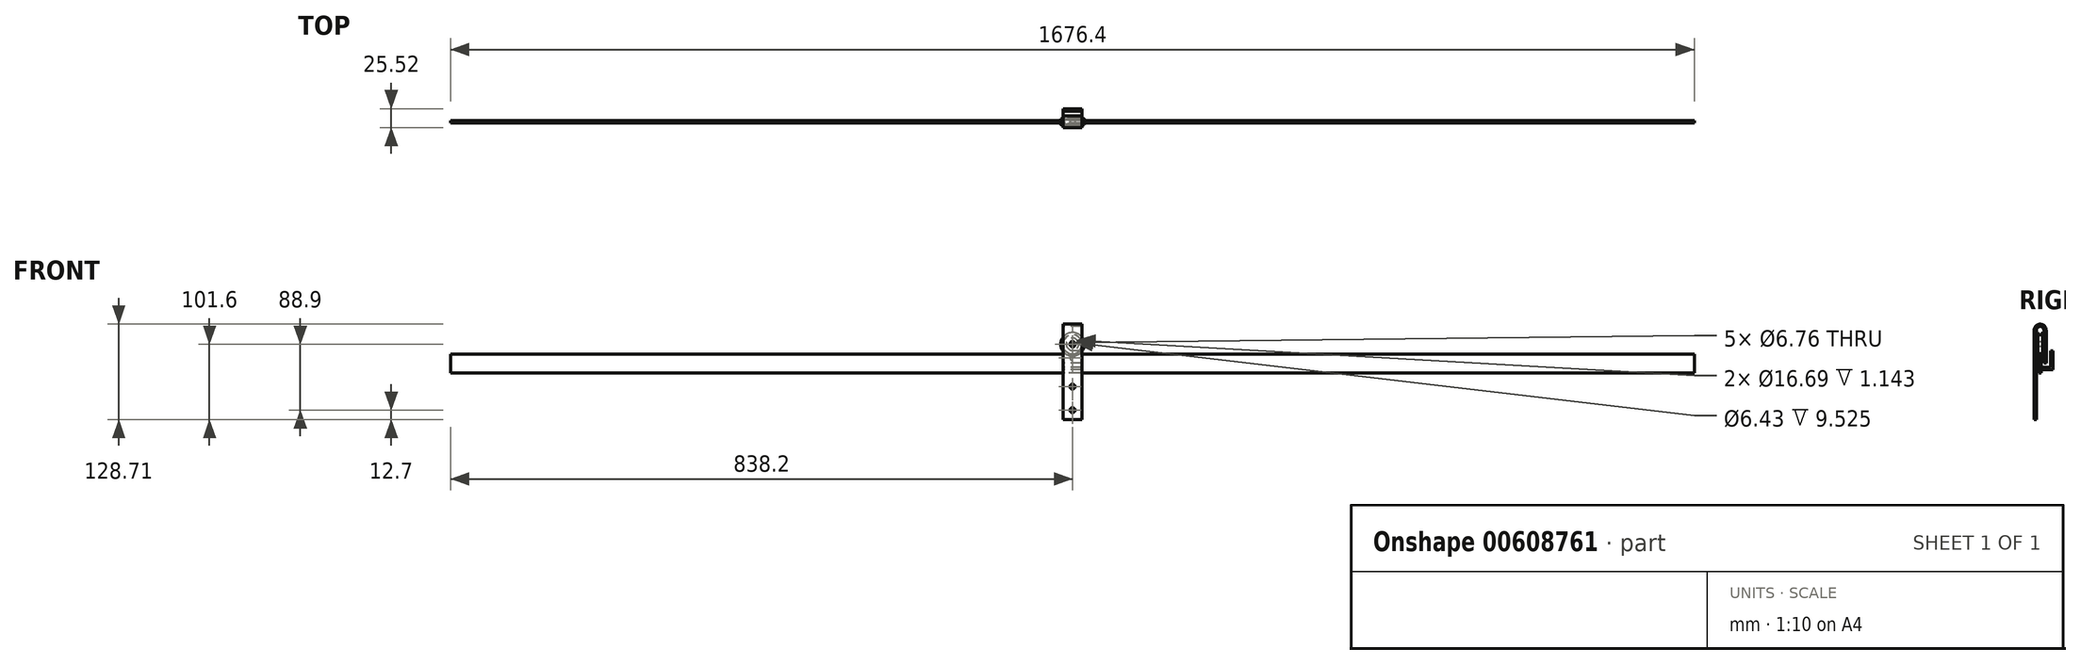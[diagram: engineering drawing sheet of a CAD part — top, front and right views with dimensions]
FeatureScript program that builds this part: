
annotation { "Feature Type Name" : "Feature", "Feature Type Description" : "" }
export const myFeature = defineFeature(function(context is Context, id is Id, definition is map)
    precondition{}
    {
        {
            var Q0;
            Q0=qCreatedBy(makeId("Right.planeOp"),FACE);
            var sketch = newSketch(context, id + "F0", { "sketchPlane" : qUnion([Q0])});
            skLineSegment(sketch, "E0", {"start": v(-9, 0) * mm, "end": v(10.82, 0) * mm, "construction": true});
            skLineSegment(sketch, "E1", {"start": v(-4.76, 3.21) * mm, "end": v(4.76, 3.21) * mm});
            skLineSegment(sketch, "E2", {"start": v(4.76, 3.21) * mm, "end": v(4.76, 4.57) * mm});
            skLineSegment(sketch, "E3", {"start": v(4.76, 4.57) * mm, "end": v(2.97, 4.57) * mm});
            skLineSegment(sketch, "E4", {"start": v(2.97, 4.57) * mm, "end": v(2.97, 8.34) * mm});
            skLineSegment(sketch, "E5", {"start": v(2.97, 8.34) * mm, "end": v(4.11, 8.34) * mm});
            skLineSegment(sketch, "E6", {"start": v(4.11, 8.34) * mm, "end": v(4.11, 15.88) * mm});
            skLineSegment(sketch, "E7", {"start": v(4.11, 15.88) * mm, "end": v(2.97, 15.88) * mm});
            skLineSegment(sketch, "E8", {"start": v(0, 0) * mm, "end": v(0, 15.88) * mm, "construction": true});
            skArc(sketch, "E9", {"start": v(-2.97, 15.88) * mm, "mid": v(0, 12.9) * mm, "end": v(2.97, 15.88) * mm});
            skLineSegment(sketch, "E10", {"start": v(-2.97, 15.88) * mm, "end": v(-4.11, 15.88) * mm});
            skLineSegment(sketch, "E11", {"start": v(-4.11, 15.88) * mm, "end": v(-4.11, 8.34) * mm});
            skLineSegment(sketch, "E12", {"start": v(-4.11, 8.34) * mm, "end": v(-2.97, 8.34) * mm});
            skLineSegment(sketch, "E13", {"start": v(-2.97, 8.34) * mm, "end": v(-2.97, 4.57) * mm});
            skLineSegment(sketch, "E14", {"start": v(-2.97, 4.57) * mm, "end": v(-4.76, 4.57) * mm});
            skLineSegment(sketch, "E15", {"start": v(-4.76, 4.57) * mm, "end": v(-4.76, 3.21) * mm});
            skSolve(sketch);
        }
        {
            var Q0;
            Q0 = qSketchRegion(id + "F0", true);
            var Q1;
            Q1=sQuery(id+"F0.wireOp",EDGE,"E0");
            revolve(context, id + "F1", {"entities" : qUnion([Q0]), "axis" : qUnion([Q1]), "revolveType" : RevolveType.FULL});
        }
        {
            var Q0;
            Q0=qCreatedBy(makeId("Right.planeOp"),FACE);
            var sketch = newSketch(context, id + "F2", { "sketchPlane" : qUnion([Q0])});
            skLineSegment(sketch, "E16.bottom", {"start": v(1.59, -38.89) * mm, "end": v(-1.59, -38.89) * mm});
            skLineSegment(sketch, "E16.top", {"start": v(1.59, -13.49) * mm, "end": v(-1.59, -13.49) * mm});
            skLineSegment(sketch, "E16.left", {"start": v(1.59, -38.89) * mm, "end": v(1.59, -13.49) * mm});
            skLineSegment(sketch, "E16.right", {"start": v(-1.59, -38.89) * mm, "end": v(-1.59, -13.49) * mm});
            skPoint(sketch, "E16.middle", {"position": v(0, -26.19) * mm});
            skLineSegment(sketch, "E17", {"start": v(4.89, -25.4) * mm, "end": v(4.89, 19.05) * mm});
            skArc(sketch, "E18", {"start": v(4.89, 19.05) * mm, "mid": v(0, 23.94) * mm, "end": v(-4.89, 19.05) * mm});
            skLineSegment(sketch, "E19", {"start": v(-4.89, 19.05) * mm, "end": v(-4.89, -101.6) * mm});
            skLineSegment(sketch, "E20.0", {"start": v(-8.06, 19.05) * mm, "end": v(-8.06, -101.6) * mm});
            skArc(sketch, "E20.1", {"start": v(8.06, 19.05) * mm, "mid": v(0, 27.11) * mm, "end": v(-8.06, 19.05) * mm});
            skLineSegment(sketch, "E20.2", {"start": v(8.06, -25.4) * mm, "end": v(8.06, 19.05) * mm});
            skLineSegment(sketch, "E21", {"start": v(4.89, -25.4) * mm, "end": v(8.06, -25.4) * mm});
            skLineSegment(sketch, "E22", {"start": v(-4.89, -101.6) * mm, "end": v(-8.06, -101.6) * mm});
            skLineSegment(sketch, "E23", {"start": v(1.59, -34.12) * mm, "end": v(17.46, -34.12) * mm});
            skLineSegment(sketch, "E24", {"start": v(17.46, -34.12) * mm, "end": v(17.46, -8.72) * mm});
            skLineSegment(sketch, "E25", {"start": v(17.46, -8.72) * mm, "end": v(14.29, -8.72) * mm});
            skLineSegment(sketch, "E26", {"start": v(14.29, -8.72) * mm, "end": v(14.29, -27.77) * mm});
            skLineSegment(sketch, "E27", {"start": v(11.11, -30.95) * mm, "end": v(1.59, -30.95) * mm});
            skLineSegment(sketch, "E28", {"start": v(1.59, -30.95) * mm, "end": v(1.59, -34.12) * mm});
            skPoint(sketch, "E29.visualSharp", {"position": v(14.29, -30.95) * mm});
            skArc(sketch, "E29.filletArc", {"start": v(11.11, -30.95) * mm, "mid": v(13.36, -30.02) * mm, "end": v(14.29, -27.77) * mm});
            skSolve(sketch);
        }
        {
            var Q0;
            Q0=makeQuery(id+"F2.imprint","IMPRINT",FACE,{"disambiguationData":[TD([[makeQuery(id+"F2.imprint","IMPRINT",EDGE,{"derivedFrom":sQuery(id+"F2.wireOp",EDGE,"E16.bottom")}),-1.0]])]});
            extrude(context, id + "F3", {"entities" : qUnion([Q0]), "endBound" : BoundingType.SYMMETRIC, "depth" : 1676.4 * mm, "offsetDistance" : 25.4 * mm});
        }
        {
            var Q0;
            Q0=makeQuery(id+"F2.imprint","IMPRINT",FACE,{"disambiguationData":[TD([[makeQuery(id+"F2.imprint","IMPRINT",EDGE,{"derivedFrom":sQuery(id+"F2.wireOp",EDGE,"E17")}),-1.0]])]});
            extrude(context, id + "F4", {"entities" : qUnion([Q0]), "endBound" : BoundingType.SYMMETRIC, "depth" : 25.4 * mm, "offsetDistance" : 25.4 * mm});
        }
        {
            var Q0;
            Q0=makeQuery(id+"F2.imprint","IMPRINT",FACE,{"disambiguationData":[TD([[makeQuery(id+"F2.imprint","IMPRINT",EDGE,{"derivedFrom":sQuery(id+"F2.wireOp",EDGE,"E23")}),1.0]])]});
            extrude(context, id + "F5", {"entities" : qUnion([Q0]), "endBound" : BoundingType.SYMMETRIC, "depth" : 25.4 * mm, "offsetDistance" : 25.4 * mm});
        }
        {
            var Q0;
            Q0=makeQuery(id+"F4.opExtrude","SWEPT_FACE",FACE,{"disambiguationData":[OSD([sQuery(id+"F2.wireOp",EDGE,"E20.0")])]});
            var sketch = newSketch(context, id + "F6", { "sketchPlane" : qUnion([Q0])});
            skPoint(sketch, "E30", {"position": v(0, 0) * mm});
            skPoint(sketch, "E31", {"position": v(0, -57.15) * mm});
            skPoint(sketch, "E32", {"position": v(0, -88.9) * mm});
            skLineSegment(sketch, "E33", {"start": v(0, -57.15) * mm, "end": v(0, -88.9) * mm, "construction": true});
            skLineSegment(sketch, "E34", {"start": v(0, -57.15) * mm, "end": v(0, 0) * mm, "construction": true});
            skSolve(sketch);
        }
        {
            var Q0;
            Q0=sQuery(id+"F6.wireOp",VERTEX,"E30");
            var Q1;
            Q1=sQuery(id+"F6.wireOp",VERTEX,"E31");
            var Q2;
            Q2=sQuery(id+"F6.wireOp",VERTEX,"E32");
            var Q3;
            Q3=makeQuery(id+"F4.opExtrude","SWEPT_BODY",BODY,{"disambiguationData":[OSD([sQuery(id+"F2.wireOp",EDGE,"E17"),sQuery(id+"F2.wireOp",EDGE,"E18"),sQuery(id+"F2.wireOp",EDGE,"E19"),sQuery(id+"F2.wireOp",EDGE,"E20.0"),sQuery(id+"F2.wireOp",EDGE,"E20.1"),sQuery(id+"F2.wireOp",EDGE,"E20.2"),sQuery(id+"F2.wireOp",EDGE,"E21"),sQuery(id+"F2.wireOp",EDGE,"E22")])]});
            hole(context, id + "F7", {"style" : HoleStyle.SIMPLE, "endStyle" : HoleEndStyle.THROUGH, "standardTappedOrClearance" : lookupTablePath({ "standard" : "ANSI", "fit" : "Normal (ASME)", "size" : "1/4", "type" : "Clearance" }), "standardBlindInLast" : lookupTablePath({ "fit" : "Free", "standard" : "ANSI", "size" : "1/4", "type" : "Clearance" }), "holeDiameter" : 6.76 * mm, "majorDiameter" : 6.35 * mm, "isTappedThrough" : true, "tappedDepth" : 12.7 * mm, "tapClearance" : 3, "locations" : qUnion([Q0, Q1, Q2]), "scope" : qUnion([Q3])});
        }
        {
            var Q0;
            Q0=makeQuery(id+"F5.opExtrude","SWEPT_FACE",FACE,{"disambiguationData":[OSD([sQuery(id+"F2.wireOp",EDGE,"E24")])]});
            var sketch = newSketch(context, id + "F8", { "sketchPlane" : qUnion([Q0])});
            skPoint(sketch, "E35", {"position": v(0, -18.25) * mm});
            skLineSegment(sketch, "E36", {"start": v(0, -18.25) * mm, "end": v(0, -34.12) * mm, "construction": true});
            skSolve(sketch);
        }
        {
            var Q0;
            Q0=sQuery(id+"F8.wireOp",VERTEX,"E35");
            var Q1;
            Q1=makeQuery(id+"F5.opExtrude","SWEPT_BODY",BODY,{"disambiguationData":[OSD([sQuery(id+"F2.wireOp",EDGE,"E23"),sQuery(id+"F2.wireOp",EDGE,"E24"),sQuery(id+"F2.wireOp",EDGE,"E25"),sQuery(id+"F2.wireOp",EDGE,"E26"),sQuery(id+"F2.wireOp",EDGE,"E27"),sQuery(id+"F2.wireOp",EDGE,"E28"),sQuery(id+"F2.wireOp",EDGE,"E29.filletArc")])]});
            hole(context, id + "F9", {"style" : HoleStyle.SIMPLE, "endStyle" : HoleEndStyle.THROUGH, "standardTappedOrClearance" : lookupTablePath({ "standard" : "ANSI", "fit" : "Normal (ASME)", "size" : "1/4", "type" : "Clearance" }), "standardBlindInLast" : lookupTablePath({ "fit" : "Free", "standard" : "ANSI", "size" : "1/4", "type" : "Clearance" }), "holeDiameter" : 6.76 * mm, "majorDiameter" : 6.35 * mm, "isTappedThrough" : true, "tappedDepth" : 12.7 * mm, "tapClearance" : 3, "locations" : qUnion([Q0]), "scope" : qUnion([Q1])});
        }
    });
